# Revit family: FU_Stool_Sandler_Sella 290-61
name_source: partatom
category: Furniture
units: mm (PartAtom-declared; Revit-internal decimal feet)

## family parameters
Always vertical = Yes
Cut with Voids When Loaded = No
OmniClass Number = 23.40.20.00
OmniClass Title = General Furniture and Specialties
Room Calculation Point = No
Shared = No
Work Plane-Based = No

## types (1)
- Sella 290.61
    Default Elevation = 0 mm  [stored 0 ft]
    Depth = 460 mm  [stored 1.50919 ft]
    Description = Bar stool in matt beech with leather seat and back. Metal parts in stainless steel. Indoor use only.
    Height = 920 mm  [stored 3.01837 ft]
    Manufacturer = Sandler
    Model = Sella 290.61
    URL = https://www.sandlerseating.com
    Width = 410 mm  [stored 1.34514 ft]

note: [stored X ft] marks values corroborated as IEEE doubles in the binary element streams (Revit-internal decimal feet)

## geometry (parser evidence)
native form markers: Sweep x5
no freeform markers — native parametric forms only
